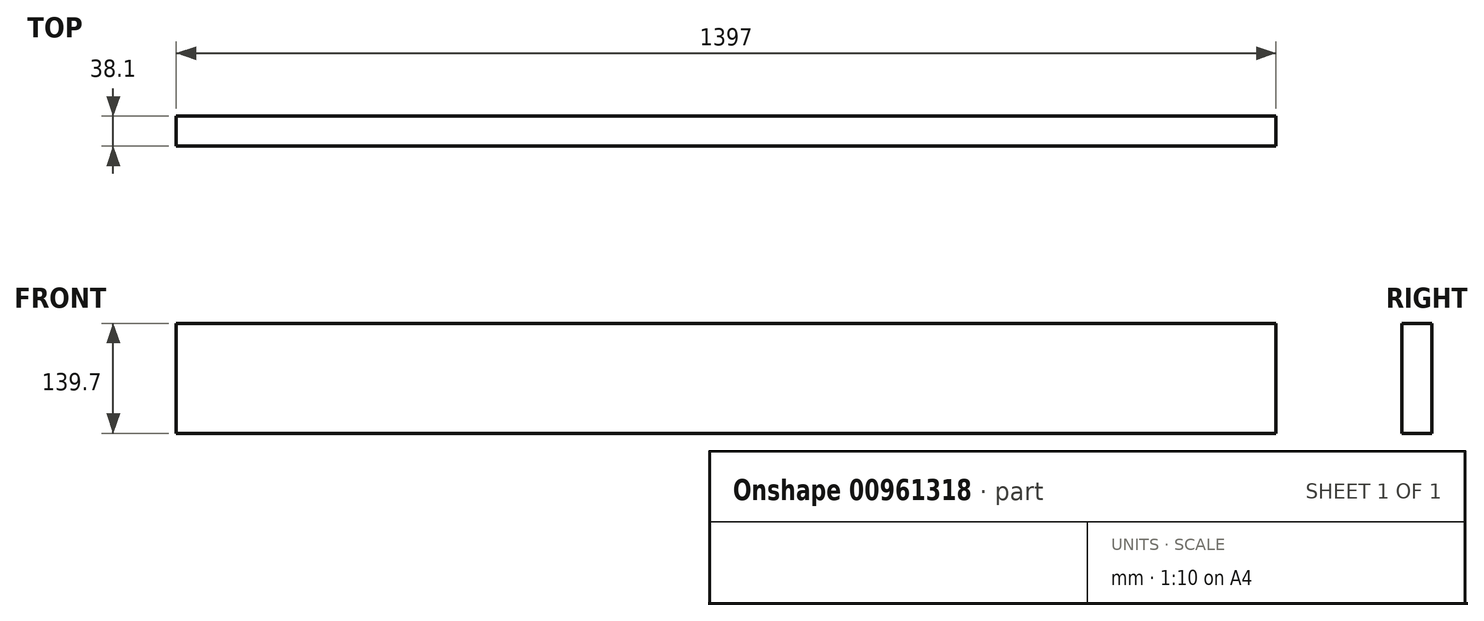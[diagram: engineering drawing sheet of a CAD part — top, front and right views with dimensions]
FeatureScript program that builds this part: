
annotation { "Feature Type Name" : "Feature", "Feature Type Description" : "" }
export const myFeature = defineFeature(function(context is Context, id is Id, definition is map)
    precondition{}
    {
        {
            var Q0;
            Q0=qCreatedBy(makeId("Right.planeOp"),FACE);
            var sketch = newSketch(context, id + "F0", { "sketchPlane" : qUnion([Q0])});
            skLineSegment(sketch, "E0.bottom", {"start": v(19.05, 69.85) * mm, "end": v(-19.05, 69.85) * mm});
            skLineSegment(sketch, "E0.top", {"start": v(19.05, -69.85) * mm, "end": v(-19.05, -69.85) * mm});
            skLineSegment(sketch, "E0.left", {"start": v(19.05, 69.85) * mm, "end": v(19.05, -69.85) * mm});
            skLineSegment(sketch, "E0.right", {"start": v(-19.05, 69.85) * mm, "end": v(-19.05, -69.85) * mm});
            skPoint(sketch, "E0.middle", {"position": v(0, 0) * mm});
            skSolve(sketch);
        }
        {
            var Q0;
            Q0=makeQuery(id+"F0.imprint","IMPRINT",FACE,{"disambiguationData":[TD([[makeQuery(id+"F0.imprint","IMPRINT",EDGE,{"derivedFrom":sQuery(id+"F0.wireOp",EDGE,"E0.bottom")}),1.0]])]});
            extrude(context, id + "F1", {"entities" : qUnion([Q0]), "endBound" : BoundingType.SYMMETRIC, "depth" : 1397 * mm, "offsetDistance" : 25.4 * mm});
        }
    });
